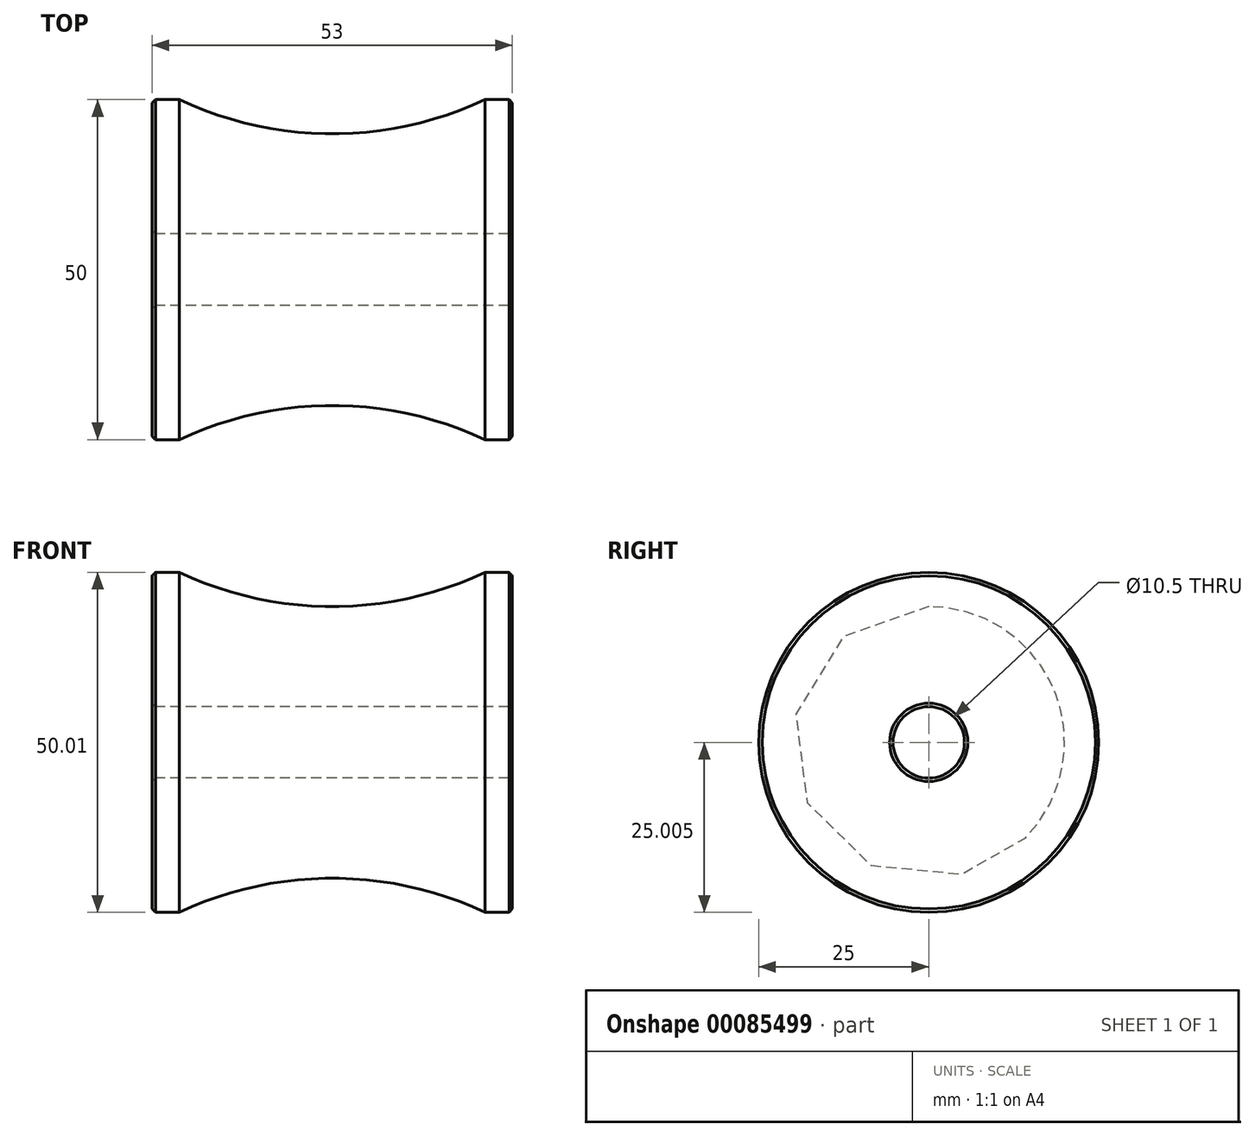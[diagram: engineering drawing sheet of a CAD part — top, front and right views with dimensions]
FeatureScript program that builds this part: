
annotation { "Feature Type Name" : "Feature", "Feature Type Description" : "" }
export const myFeature = defineFeature(function(context is Context, id is Id, definition is map)
    precondition{}
    {
        {
            var Q0;
            Q0=qCreatedBy(makeId("Front.planeOp"),FACE);
            var sketch = newSketch(context, id + "F0", { "sketchPlane" : qUnion([Q0])});
            skLineSegment(sketch, "E0.bottom", {"start": v(26.5, 9.87) * mm, "end": v(-26.5, 9.87) * mm});
            skLineSegment(sketch, "E0.top", {"start": v(26.5, -9.87) * mm, "end": v(22.5, -9.87) * mm});
            skLineSegment(sketch, "E0.left", {"start": v(26.5, 9.87) * mm, "end": v(26.5, -9.87) * mm});
            skLineSegment(sketch, "E0.right", {"start": v(-26.5, 9.87) * mm, "end": v(-26.5, -9.87) * mm});
            skPoint(sketch, "E0.middle", {"position": v(0, 0) * mm});
            skLineSegment(sketch, "E1.top", {"start": v(-26.5, 15.12) * mm, "end": v(26.5, 15.13) * mm, "construction": true});
            skPoint(sketch, "E2", {"position": v(-22.5, -9.87) * mm});
            skPoint(sketch, "E3", {"position": v(-26.5, -9.87) * mm});
            skPoint(sketch, "E4", {"position": v(22.5, -9.87) * mm});
            skPoint(sketch, "E5.third.point", {"position": v(0, -4.85) * mm});
            skLineSegment(sketch, "E6.trimOffspring", {"start": v(-22.5, -9.87) * mm, "end": v(-26.5, -9.87) * mm});
            skArc(sketch, "E7", {"start": v(22.5, -9.88) * mm, "mid": v(0, -4.85) * mm, "end": v(-22.5, -9.88) * mm});
            skPoint(sketch, "E7.third.point", {"position": v(19.36, -8.52) * mm});
            skSolve(sketch);
        }
        {
            var Q0;
            Q0=qCreatedBy(makeId("Front.planeOp"),FACE);
            var sketch = newSketch(context, id + "F1", { "sketchPlane" : qUnion([Q0])});
            skPoint(sketch, "E8", {"position": v(0, -4.86) * mm});
            skPoint(sketch, "E9", {"position": v(0, 15.14) * mm});
            skArc(sketch, "E10", {"start": v(22.44, -9.95) * mm, "mid": v(0.14, -4.86) * mm, "end": v(-22.24, -9.54) * mm});
            skPoint(sketch, "E10.first.point", {"position": v(-22.24, -9.54) * mm});
            skPoint(sketch, "E10.second.point", {"position": v(22.44, -9.95) * mm});
            skSolve(sketch);
        }
        {
            var Q0;
            Q0 = qSketchRegion(id + "F1", true);
            var Q1;
            Q1=makeQuery(id+"F0.imprint","IMPRINT",FACE,{"disambiguationData":[TD([[makeQuery(id+"F0.imprint","IMPRINT",EDGE,{"derivedFrom":sQuery(id+"F0.wireOp",EDGE,"E0.bottom")}),1.0]])]});
            var Q2;
            Q2=sQuery(id+"F0.wireOp",EDGE,"E1.top");
            revolve(context, id + "F2", {"entities" : qUnion([Q0, Q1]), "axis" : qUnion([Q2]), "revolveType" : RevolveType.FULL});
        }
        {
            var Q0;
            Q0=makeQuery(id+"F2.opRevolve","SWEPT_EDGE",EDGE,{"disambiguationData":[OSD([sQuery(id+"F0.wireOp",EDGE,"E0.top"),sQuery(id+"F0.wireOp",EDGE,"E0.left")])]});
            var Q1;
            Q1=makeQuery(id+"F2.opRevolve","SWEPT_EDGE",EDGE,{"disambiguationData":[OSD([sQuery(id+"F0.wireOp",EDGE,"E0.right"),sQuery(id+"F0.wireOp",EDGE,"E6.trimOffspring")])]});
            chamfer(context, id + "F3", {"entities" : qUnion([Q0, Q1]), "width" : .5 * mm, "tangentPropagation" : true});
        }
        {
            var Q0;
            Q0=makeQuery(id+"F2.opRevolve","SWEPT_EDGE",EDGE,{"disambiguationData":[OSD([sQuery(id+"F0.wireOp",EDGE,"E0.bottom"),sQuery(id+"F0.wireOp",EDGE,"E0.left")])]});
            var Q1;
            Q1=makeQuery(id+"F2.opRevolve","SWEPT_EDGE",EDGE,{"disambiguationData":[OSD([sQuery(id+"F0.wireOp",EDGE,"E0.bottom"),sQuery(id+"F0.wireOp",EDGE,"E0.right")])]});
            chamfer(context, id + "F4", {"entities" : qUnion([Q0, Q1]), "chamferType" : ChamferType.OFFSET_ANGLE, "width" : .5 * mm, "oppositeDirection" : false, "angle" : 45 * degree});
        }
    });
